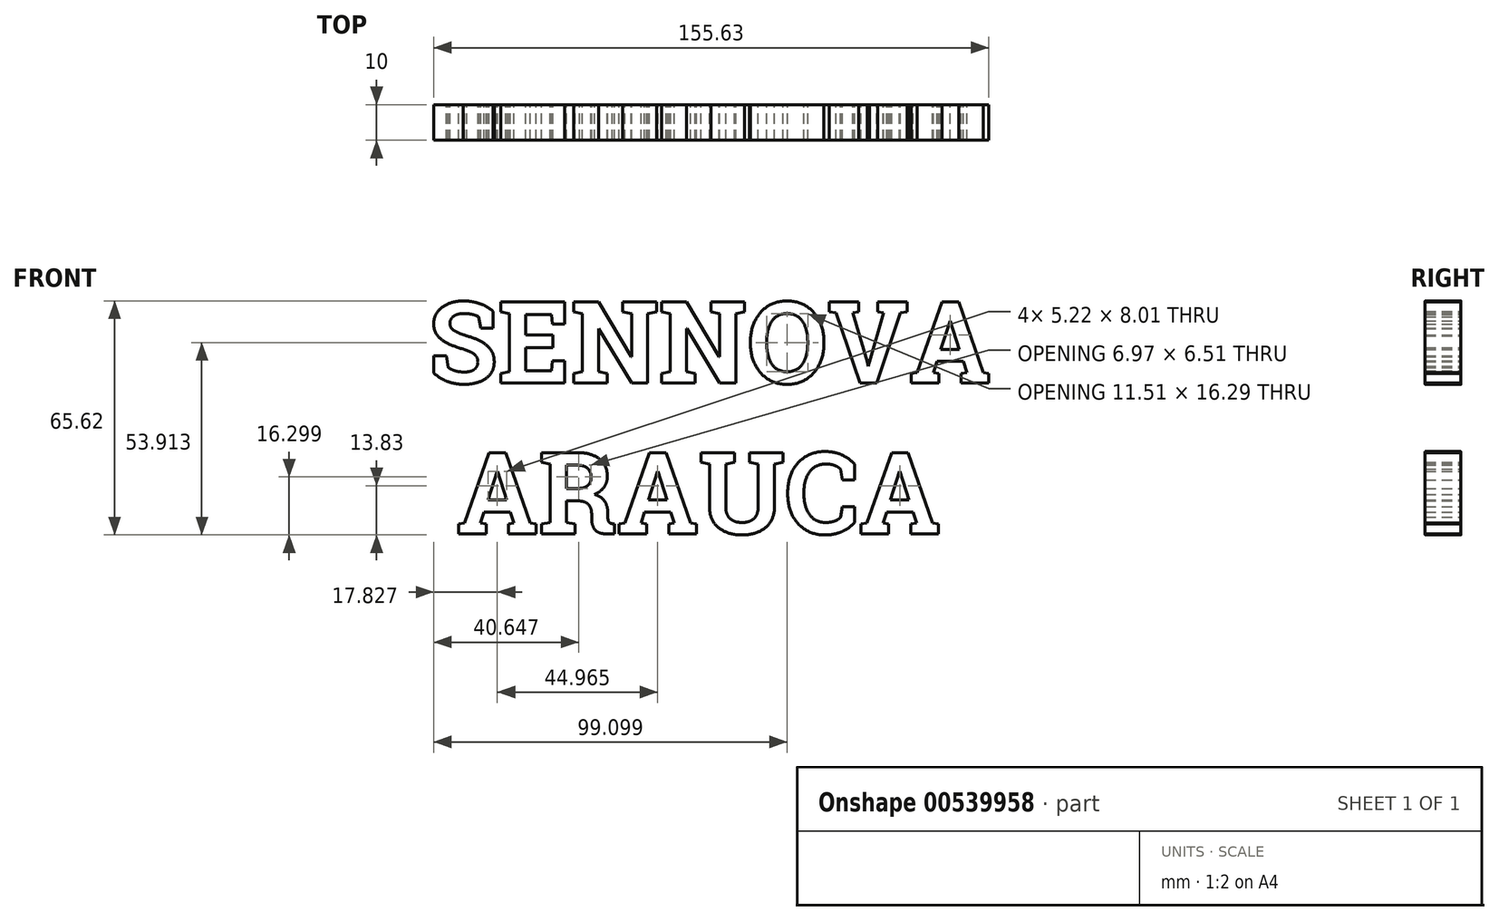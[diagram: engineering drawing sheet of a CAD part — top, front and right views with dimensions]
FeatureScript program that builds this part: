
annotation { "Feature Type Name" : "Feature", "Feature Type Description" : "" }
export const myFeature = defineFeature(function(context is Context, id is Id, definition is map)
    precondition{}
    {
        {
            var Q0;
            Q0=qCreatedBy(makeId("Front.planeOp"),FACE);
            var sketch = newSketch(context, id + "F0", { "sketchPlane" : qUnion([Q0])});
            skText(sketch, "E0", { "text": "SENNOVA\n ARAUCA", "fontName": "RobotoSlab-Bold.ttf"});
            const initialGuessF0  = {"E0": [-0.07187, 0.03884, 1, 0, 0.02303]};
            skSetInitialGuess(sketch, initialGuessF0);
            skSolve(sketch);
        }
        {
            var Q0;
            Q0 = qSketchRegion(id + "F0", true);
            extrude(context, id + "F1", {"entities" : qUnion([Q0]), "depth" : 10 * mm, "offsetDistance" : 25 * mm});
        }
    });
